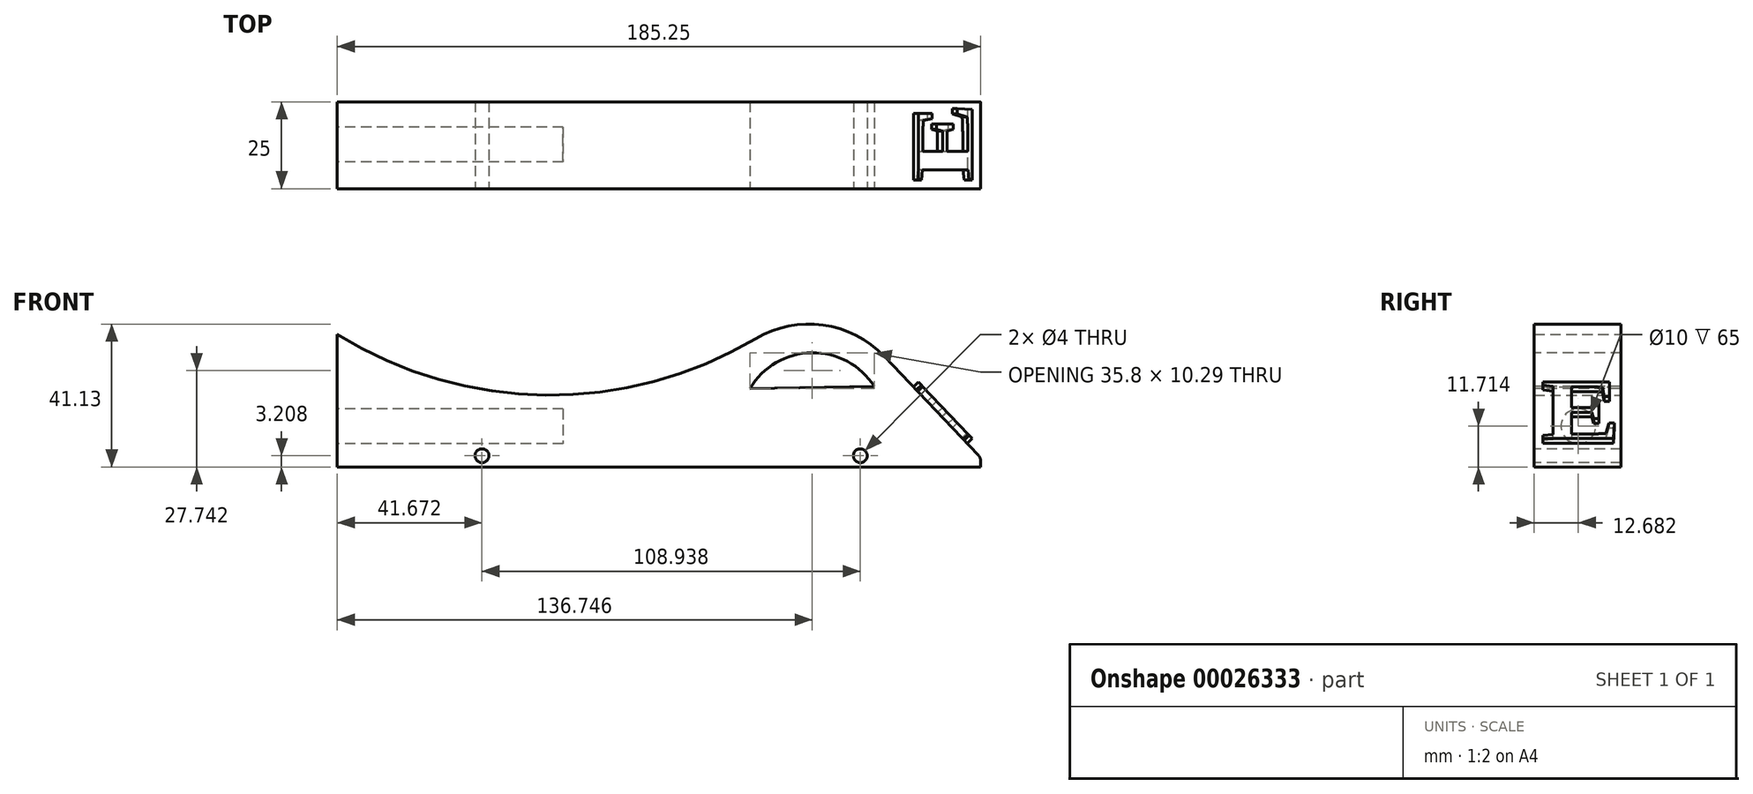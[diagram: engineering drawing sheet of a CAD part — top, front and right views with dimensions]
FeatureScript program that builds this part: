
annotation { "Feature Type Name" : "Feature", "Feature Type Description" : "" }
export const myFeature = defineFeature(function(context is Context, id is Id, definition is map)
    precondition{}
    {
        {
            var Q0;
            Q0=qCreatedBy(makeId("Front.planeOp"),FACE);
            var sketch = newSketch(context, id + "F0", { "sketchPlane" : qUnion([Q0])});
            skLineSegment(sketch, "E0", {"start": v(-122.9, -19.78) * mm, "end": v(34.29, -19.78) * mm});
            skLineSegment(sketch, "E1", {"start": v(34.64, -18.07) * mm, "end": v(34.64, -19.43) * mm});
            skPoint(sketch, "E2.visualSharp", {"position": v(-143.74, 3.92) * mm});
            skPoint(sketch, "E3.visualSharp", {"position": v(34.64, 10.22) * mm});
            skArc(sketch, "E4", {"start": v(-150.6, 18.38) * mm, "mid": v(-90.54, 0.89) * mm, "end": v(-30.12, 17.14) * mm});
            skLineSegment(sketch, "E5", {"start": v(6.92, 12.04) * mm, "end": v(33.95, -16.35) * mm});
            skPoint(sketch, "E6.visualSharp", {"position": v(-11.25, 31.11) * mm});
            skArc(sketch, "E6.filletArc", {"start": v(6.92, 12.04) * mm, "mid": v(-10.71, 21.07) * mm, "end": v(-30.12, 17.14) * mm});
            skPoint(sketch, "E7.visualSharp", {"position": v(6.92, 12.04) * mm});
            skLineSegment(sketch, "E7.filletArc", {"start": v(6.92, 12.04) * mm, "end": v(6.92, 12.04) * mm});
            skArc(sketch, "E8.filletArc", {"start": v(34.64, -18.07) * mm, "mid": v(34.46, -17.14) * mm, "end": v(33.95, -16.35) * mm});
            skLineSegment(sketch, "E9", {"start": v(34.64, -19.43) * mm, "end": v(34.64, -19.78) * mm});
            skLineSegment(sketch, "E10", {"start": v(34.64, -19.78) * mm, "end": v(34.29, -19.78) * mm});
            skLineSegment(sketch, "E11", {"start": v(-122.9, -19.78) * mm, "end": v(-150.6, -19.78) * mm});
            skLineSegment(sketch, "E12", {"start": v(-150.6, 18.38) * mm, "end": v(-150.6, -19.78) * mm});
            skSolve(sketch);
        }
        {
            var Q0;
            Q0=makeQuery(id+"F0.imprint","IMPRINT",FACE,{"disambiguationData":[TD([[makeQuery(id+"F0.imprint","IMPRINT",EDGE,{"derivedFrom":sQuery(id+"F0.wireOp",EDGE,"E0")}),1.0]])]});
            extrude(context, id + "F1", {"entities" : qUnion([Q0]), "depth" : 25 * mm});
        }
        {
            var Q0;
            Q0=makeQuery(id+"F1.opExtrude","CAP_FACE",FACE,{"disambiguationData":[OSD([sQuery(id+"F0.wireOp",EDGE,"E0"),sQuery(id+"F0.wireOp",EDGE,"6e4099fd-0cd3-4de4-85de-8c050abf150f"),sQuery(id+"F0.wireOp",EDGE,"E1"),sQuery(id+"F0.wireOp",EDGE,"E2.filletArc"),sQuery(id+"F0.wireOp",EDGE,"bb62e975-a215-4ff5-a1c8-8dd1521318f1.filletArc"),sQuery(id+"F0.wireOp",EDGE,"E4"),sQuery(id+"F0.wireOp",EDGE,"E5"),sQuery(id+"F0.wireOp",EDGE,"E6.filletArc"),sQuery(id+"F0.wireOp",EDGE,"fc66d5d4-d66c-4578-aa7c-df8725a15dc5.filletArc"),sQuery(id+"F0.wireOp",EDGE,"E8.filletArc"),sQuery(id+"F0.wireOp",EDGE,"d60d9177-7f5e-4e0c-8f93-6fc0853f03ef.filletArc")])],"isStart":false});
            var sketch = newSketch(context, id + "F2", { "sketchPlane" : qUnion([Q0])});
            skCircle(sketch, "E13", {"center": v(0, -16.57) * mm, "radius": 2 * mm});
            skCircle(sketch, "E14", {"center": v(-108.94, -16.57) * mm, "radius": 2 * mm});
            skSolve(sketch);
        }
        {
            var Q0;
            Q0=makeQuery(id+"F2.imprint","IMPRINT",FACE,{"disambiguationData":[TD([[makeQuery(id+"F2.imprint","IMPRINT",EDGE,{"derivedFrom":sQuery(id+"F2.wireOp",EDGE,"E13")}),-1.0]])]});
            var sketch = newSketch(context, id + "F3", { "sketchPlane" : qUnion([Q0])});
            skSolve(sketch);
        }
        {
            var Q0;
            Q0=makeQuery(id+"F2.imprint","IMPRINT",FACE,{"disambiguationData":[TD([[makeQuery(id+"F2.imprint","IMPRINT",EDGE,{"derivedFrom":sQuery(id+"F2.wireOp",EDGE,"E13")}),-1.0]])]});
            var sketch = newSketch(context, id + "F4", { "sketchPlane" : qUnion([Q0])});
            skArc(sketch, "E15", {"start": v(4.04, 3.4) * mm, "mid": v(-14.03, 13.1) * mm, "end": v(-31.76, 2.82) * mm});
            skLineSegment(sketch, "E16", {"start": v(4.04, 3.4) * mm, "end": v(-31.76, 2.82) * mm});
            skSolve(sketch);
        }
        {
            var Q0;
            Q0=makeQuery(id+"F4.imprint","IMPRINT",FACE,{"disambiguationData":[TD([[makeQuery(id+"F4.imprint","IMPRINT",EDGE,{"derivedFrom":sQuery(id+"F4.wireOp",EDGE,"E15")}),1.0]])]});
            extrude(context, id + "F5", {"entities" : qUnion([Q0]), "operationType" : NewBodyOperationType.REMOVE, "endBound" : BoundingType.THROUGH_ALL, "oppositeDirection" : true, "depth" : 25 * mm});
        }
        {
            var Q0;
            Q0=makeQuery(id+"F1.opExtrude","SWEPT_FACE",FACE,{"disambiguationData":[OSD([sQuery(id+"F0.wireOp",EDGE,"E5")])]});
            var sketch = newSketch(context, id + "F6", { "sketchPlane" : qUnion([Q0])});
            skText(sketch, "E17", { "text": "E", "fontName": "Tinos-Bold.ttf"});
            const initialGuessF6  = {"E17": [-0.02304, -0.03064, 1, 0, 0.02469]};
            skSetInitialGuess(sketch, initialGuessF6);
            skSolve(sketch);
        }
        {
            var Q0;
            Q0=makeQuery(id+"F6.imprint","IMPRINT",FACE,{"disambiguationData":[TD([[makeQuery(id+"F6.imprint","IMPRINT",EDGE,{"derivedFrom":sQuery(id+"F6.wireOp",EDGE,"E17.sketch_text.stroke-0")}),-1.0]])]});
            extrude(context, id + "F7", {"entities" : qUnion([Q0]), "operationType" : NewBodyOperationType.ADD, "depth" : 2 * mm});
        }
        {
            var Q0;
            Q0=makeQuery(id+"F2.imprint","IMPRINT",FACE,{"disambiguationData":[TD([[makeQuery(id+"F2.imprint","IMPRINT",EDGE,{"derivedFrom":sQuery(id+"F2.wireOp",EDGE,"E14")}),1.0]])]});
            extrude(context, id + "F8", {"entities" : qUnion([Q0]), "operationType" : NewBodyOperationType.REMOVE, "endBound" : BoundingType.THROUGH_ALL, "oppositeDirection" : true, "depth" : 25 * mm});
        }
        {
            var Q0;
            Q0=makeQuery(id+"F3.imprint","IMPRINT",FACE,{"disambiguationData":[TD([[makeQuery(id+"F3.imprint","IMPRINT",EDGE,{"derivedFrom":makeQuery(id+"F2.imprint","IMPRINT",EDGE,{"derivedFrom":sQuery(id+"F2.wireOp",EDGE,"E13")})}),1.0]])]});
            extrude(context, id + "F9", {"entities" : qUnion([Q0]), "operationType" : NewBodyOperationType.REMOVE, "endBound" : BoundingType.THROUGH_ALL, "oppositeDirection" : true, "depth" : 25 * mm});
        }
        {
            var Q0;
            Q0=makeQuery(id+"F1.opExtrude","SWEPT_FACE",FACE,{"disambiguationData":[OSD([sQuery(id+"F0.wireOp",EDGE,"E12")])]});
            var sketch = newSketch(context, id + "F10", { "sketchPlane" : qUnion([Q0])});
            skCircle(sketch, "E18", {"center": v(12.32, -8.07) * mm, "radius": 5 * mm});
            skSolve(sketch);
        }
        {
            var Q0;
            Q0=makeQuery(id+"F10.imprint","IMPRINT",FACE,{"disambiguationData":[TD([[makeQuery(id+"F10.imprint","IMPRINT",EDGE,{"derivedFrom":sQuery(id+"F10.wireOp",EDGE,"E18")}),1.0]])]});
            extrude(context, id + "F11", {"entities" : qUnion([Q0]), "operationType" : NewBodyOperationType.REMOVE, "oppositeDirection" : true, "depth" : 65 * mm});
        }
    });
